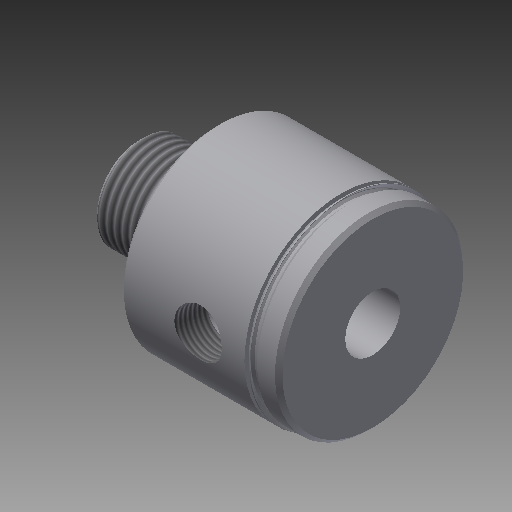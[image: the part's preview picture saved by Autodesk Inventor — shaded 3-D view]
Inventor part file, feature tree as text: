
AUTODESK INVENTOR PART (.ipt)
format: ipt  version: 2019.4 (Build 234330000, 330)  size: 295,424 bytes
history: native  units: in
note: dims shown in document units (in); Inventor stores cm internally (conversion verified against a paired STEP export)
features: other x119, sketch x5, revolve x4, thread x2, hole x1
ambient origin geometry x8: Origin, YZ Plane, XZ Plane, XY Plane, X Axis, Y Axis, Z Axis, Center Point
bodies: Solid1 (feature_tree)
feature tree (131):
  revolve  "Revolution1"  [1 undecoded]
  thread  "Thread1"  [1 undecoded]
  revolve  "Revolution2"  Angle=360.0deg
  hole  "Hole1"  [1 undecoded]
  revolve  "Revolution3"  [1 undecoded]
  thread  "Thread2"  [1 undecoded]
  revolve  "Revolution4"  [1 undecoded]
  other  "dp1_XY"
  other  "dp1_YZ"
  other  "dp1_ZX"
  other  "dp1_X"
  other  "dp1_Y"
  other  "dp1_Z"
  other  "dp1_Center"
  other  "dp2_XY"
  other  "dp2_YZ"
  other  "dp2_ZX"
  other  "dp2_X"
  other  "dp2_Y"
  other  "dp2_Z"
  other  "dp2_Center"
  other  "hh_XY"
  other  "hh_YZ"
  other  "hh_ZX"
  other  "hh_X"
  other  "hh_Y"
  other  "hh_Z"
  other  "hh_Center"
  other  "port_XY"
  other  "port_YZ"
  other  "port_ZX"
  other  "port_X"
  other  "port_Y"
  other  "port_Z"
  other  "port_Center"
  other  "rod_guide_XY"
  other  "rod_guide_YZ"
  other  "rod_guide_ZX"
  other  "rod_guide_X"
  other  "rod_guide_Y"
  other  "rod_guide_Z"
  other  "rod_guide_Center"
  other  "s1_XY"
  other  "s1_YZ"
  other  "s1_ZX"
  other  "s1_X"
  other  "s1_Y"
  other  "s1_Z"
  other  "s1_Center"
  other  "s2_XY"
  other  "s2_YZ"
  other  "s2_ZX"
  other  "s2_X"
  other  "s2_Y"
  other  "s2_Z"
  other  "s2_Center"
  other  "t1_XY"
  other  "t1_YZ"
  other  "t1_ZX"
  other  "t1_X"
  other  "t1_Y"
  other  "t1_Z"
  other  "t1_Center"
  other  "t111_XY"
  other  "t111_YZ"
  other  "t111_ZX"
  other  "t111_X"
  other  "t111_Y"
  other  "t111_Z"
  other  "t111_Center"
  other  "to_foot_bracket_XY"
  other  "to_foot_bracket_YZ"
  other  "to_foot_bracket_ZX"
  other  "to_foot_bracket_X"
  other  "to_foot_bracket_Y"
  other  "to_foot_bracket_Z"
  other  "to_foot_bracket_Center"
  other  "to_nut_XY"
  other  "to_nut_YZ"
  other  "to_nut_ZX"
  other  "to_nut_X"
  other  "to_nut_Y"
  other  "to_nut_Z"
  other  "to_nut_Center"
  other  "to_rod_XY"
  other  "to_rod_YZ"
  other  "to_rod_ZX"
  other  "to_rod_X"
  other  "to_rod_Y"
  other  "to_rod_Z"
  other  "to_rod_Center"
  other  "to_screw_XY"
  other  "to_screw_YZ"
  other  "to_screw_ZX"
  other  "to_screw_X"
  other  "to_screw_Y"
  other  "to_screw_Z"
  other  "to_screw_Center"
  other  "to_trunnion_brackets_XY"
  other  "to_trunnion_brackets_YZ"
  other  "to_trunnion_brackets_ZX"
  other  "to_trunnion_brackets_X"
  other  "to_trunnion_brackets_Y"
  other  "to_trunnion_brackets_Z"
  other  "to_trunnion_brackets_Center"
  other  "to_trunnion_brackets1_XY"
  other  "to_trunnion_brackets1_YZ"
  other  "to_trunnion_brackets1_ZX"
  other  "to_trunnion_brackets1_X"
  other  "to_trunnion_brackets1_Y"
  other  "to_trunnion_brackets1_Z"
  other  "to_trunnion_brackets1_Center"
  other  "to_trunnion_brackets2_XY"
  other  "to_trunnion_brackets2_YZ"
  other  "to_trunnion_brackets2_ZX"
  other  "to_trunnion_brackets2_X"
  other  "to_trunnion_brackets2_Y"
  other  "to_trunnion_brackets2_Z"
  other  "to_trunnion_brackets2_Center"
  other  "to_tube_XY"
  other  "to_tube_YZ"
  other  "to_tube_ZX"
  other  "to_tube_X"
  other  "to_tube_Y"
  other  "to_tube_Z"
  other  "to_tube_Center"
  sketch  "Sketch_2"  dims[d0=360.0deg d1=0.3297in d2=0.0in d3=360.0deg]
  sketch  "Sketch_3"  dims[d4=0.442in d5=0.75in d6=0.502in d7=0.25in d8=90.0deg d9=1.875in d10=0.0in d11=360.0deg]
  sketch  "Sketch3"  dims[d12=0.2521in d13=0.0in d14=360.0deg]
  sketch  "Sketch_40"  dims[d15=0.0in d16=0.0in d17=0.0in d18=0.0in d19=0.0in d20=0.0in]
  sketch  "Sketch_47"
note: 6 required parameter values undecoded (feature->parameter linkage not recoverable at this tier; creation-order binding heuristic only, values carry confidence <= 0.55)